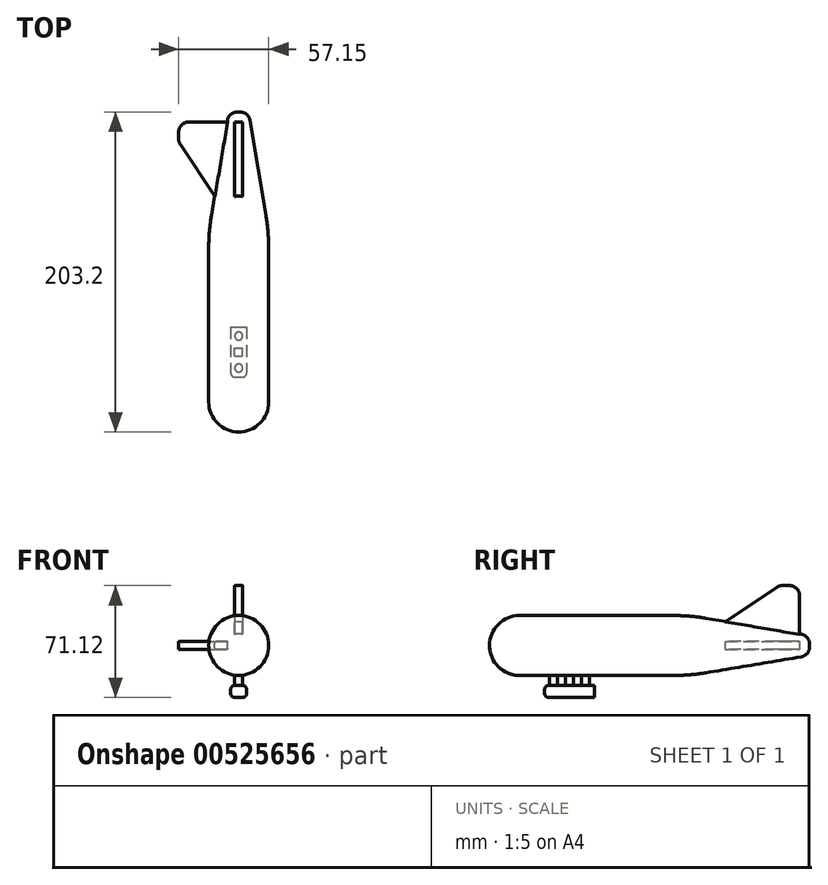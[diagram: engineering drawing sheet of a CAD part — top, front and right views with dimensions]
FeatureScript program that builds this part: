
annotation { "Feature Type Name" : "Feature", "Feature Type Description" : "" }
export const myFeature = defineFeature(function(context is Context, id is Id, definition is map)
    precondition{}
    {
        {
            var Q0;
            Q0=qCreatedBy(makeId("Front.planeOp"),FACE);
            var sketch = newSketch(context, id + "F0", { "sketchPlane" : qUnion([Q0])});
            skCircle(sketch, "E0", {"center": v(0, 0) * mm, "radius": 19.05 * mm});
            skSolve(sketch);
        }
        {
            var Q0;
            Q0=makeQuery(id+"F0.imprint","IMPRINT",FACE,{"disambiguationData":[TD([[makeQuery(id+"F0.imprint","IMPRINT",EDGE,{"derivedFrom":sQuery(id+"F0.wireOp",EDGE,"E0")}),1.0]])]});
            extrude(context, id + "F1", {"entities" : qUnion([Q0]), "endBound" : BoundingType.SYMMETRIC, "depth" : 203.2 * mm, "offsetDistance" : 25.4 * mm});
        }
        {
            var Q0;
            Q0=makeQuery(id+"F1.opExtrude","CAP_FACE",FACE,{"disambiguationData":[OSD([sQuery(id+"F0.wireOp",EDGE,"E0")])],"isStart":false});
            fillet(context, id + "F2", {"entities" : qUnion([Q0]), "radius" : 19.05 * mm, "tangentPropagation" : true, "allowEdgeOverflow" : false});
        }
        {
            var Q0;
            Q0=makeQuery(id+"F1.opExtrude","CAP_FACE",FACE,{"disambiguationData":[OSD([sQuery(id+"F0.wireOp",EDGE,"E0")])],"isStart":true});
            chamfer(context, id + "F3", {"entities" : qUnion([Q0]), "chamferType" : ChamferType.TWO_OFFSETS, "width1" : 76.2 * mm, "oppositeDirection" : false, "width2" : 12.7 * mm, "tangentPropagation" : true});
        }
        {
            var Q0;
            Q0=makeQuery(id+"F1.opExtrude","CAP_FACE",FACE,{"disambiguationData":[OSD([sQuery(id+"F0.wireOp",EDGE,"E0")])],"isStart":true});
            fillet(context, id + "F4", {"entities" : qUnion([Q0]), "radius" : 6.35 * mm, "tangentPropagation" : true, "allowEdgeOverflow" : false});
        }
        {
            var Q0;
            {var subQ0=sQuery(id+"F0.wireOp",EDGE,"E0");Q0=makeQuery(id+"F3.opChamfer","BLEND_EDGE",EDGE,{"blendedFrom":[makeQuery(id+"F1.opExtrude","CAP_EDGE",EDGE,{"disambiguationData":[OSD([subQ0])],"isStart":true}),makeQuery(id+"F1.opExtrude","SWEPT_FACE",FACE,{"disambiguationData":[OSD([subQ0])]})],"blendedInto":[makeQuery(id+"F1.opExtrude","SWEPT_FACE",FACE,{"disambiguationData":[OSD([subQ0])]})]});}
            fillet(context, id + "F5", {"entities" : qUnion([Q0]), "radius" : 127 * mm, "tangentPropagation" : true, "allowEdgeOverflow" : false});
        }
        {
            var Q0;
            Q0=qCreatedBy(makeId("Top.planeOp"),FACE);
            var sketch = newSketch(context, id + "F6", { "sketchPlane" : qUnion([Q0])});
            skLineSegment(sketch, "E1.bottom", {"start": v(-2.54, -48.26) * mm, "end": v(2.54, -48.26) * mm});
            skLineSegment(sketch, "E1.top", {"start": v(-2.54, -53.34) * mm, "end": v(2.54, -53.34) * mm});
            skLineSegment(sketch, "E1.left", {"start": v(-2.54, -48.26) * mm, "end": v(-2.54, -53.34) * mm});
            skLineSegment(sketch, "E1.right", {"start": v(2.54, -48.26) * mm, "end": v(2.54, -53.34) * mm});
            skPoint(sketch, "E1.middle", {"position": v(0, -50.8) * mm});
            skCircle(sketch, "E2", {"center": v(0, -60.96) * mm, "radius": 2.54 * mm});
            skCircle(sketch, "E3", {"center": v(0, -40.64) * mm, "radius": 2.54 * mm});
            skSolve(sketch);
        }
        {
            var Q0;
            Q0 = qSketchRegion(id + "F6", true);
            extrude(context, id + "F7", {"entities" : qUnion([Q0]), "operationType" : NewBodyOperationType.ADD, "oppositeDirection" : true, "depth" : 25.4 * mm, "offsetDistance" : 25.4 * mm});
        }
        {
            var Q0;
            Q0=makeQuery(id+"F7.opExtrude","CAP_FACE",FACE,{"disambiguationData":[OSD([sQuery(id+"F6.wireOp",EDGE,"E1.bottom"),sQuery(id+"F6.wireOp",EDGE,"E1.top"),sQuery(id+"F6.wireOp",EDGE,"E1.left"),sQuery(id+"F6.wireOp",EDGE,"E1.right")])],"isStart":false});
            var sketch = newSketch(context, id + "F8", { "sketchPlane" : qUnion([Q0])});
            skLineSegment(sketch, "E4.bottom", {"start": v(-5.08, 34.92) * mm, "end": v(5.08, 34.92) * mm});
            skLineSegment(sketch, "E4.top", {"start": v(-5.08, 66.67) * mm, "end": v(5.08, 66.67) * mm});
            skLineSegment(sketch, "E4.left", {"start": v(-5.08, 34.92) * mm, "end": v(-5.08, 66.67) * mm});
            skLineSegment(sketch, "E4.right", {"start": v(5.08, 34.92) * mm, "end": v(5.08, 66.67) * mm});
            skPoint(sketch, "E4.middle", {"position": v(0, 50.8) * mm});
            skPoint(sketch, "E4.middle.positionSnap0", {"position": v(2.54, 50.8) * mm});
            skPoint(sketch, "E4.middle.positionSnap1", {"position": v(0, 48.26) * mm});
            skPoint(sketch, "E4.centerSnap0", {"position": v(2.54, 50.8) * mm});
            skPoint(sketch, "E4.centerSnap1", {"position": v(0, 48.26) * mm});
            skSolve(sketch);
        }
        {
            var Q0;
            Q0 = qSketchRegion(id + "F8", true);
            extrude(context, id + "F9", {"entities" : qUnion([Q0]), "operationType" : NewBodyOperationType.ADD, "depth" : 7.62 * mm, "offsetDistance" : 25.4 * mm});
        }
        {
            var Q0;
            Q0=makeQuery(id+"F9.opExtrude","CAP_EDGE",EDGE,{"disambiguationData":[OSD([sQuery(id+"F8.wireOp",EDGE,"E4.left")])],"isStart":false});
            var Q1;
            Q1=makeQuery(id+"F9.opExtrude","CAP_EDGE",EDGE,{"disambiguationData":[OSD([sQuery(id+"F8.wireOp",EDGE,"E4.left")])],"isStart":true});
            var Q2;
            Q2=makeQuery(id+"F9.opExtrude","CAP_EDGE",EDGE,{"disambiguationData":[OSD([sQuery(id+"F8.wireOp",EDGE,"E4.right")])],"isStart":true});
            var Q3;
            Q3=makeQuery(id+"F9.opExtrude","CAP_EDGE",EDGE,{"disambiguationData":[OSD([sQuery(id+"F8.wireOp",EDGE,"E4.right")])],"isStart":false});
            fillet(context, id + "F10", {"entities" : qUnion([Q0, Q1, Q2, Q3]), "radius" : 2.54 * mm, "tangentPropagation" : true, "allowEdgeOverflow" : false});
        }
        {
            var Q0;
            Q0=makeQuery(id+"F9.opExtrude","SWEPT_FACE",FACE,{"disambiguationData":[OSD([sQuery(id+"F8.wireOp",EDGE,"E4.top")])]});
            fillet(context, id + "F11", {"entities" : qUnion([Q0]), "radius" : 2.54 * mm, "tangentPropagation" : true, "allowEdgeOverflow" : false});
        }
        {
            var Q0;
            Q0=qCreatedBy(makeId("Right.planeOp"),FACE);
            var sketch = newSketch(context, id + "F12", { "sketchPlane" : qUnion([Q0])});
            skLineSegment(sketch, "E5", {"start": v(25.4, 0) * mm, "end": v(95.25, 0) * mm});
            skLineSegment(sketch, "E6", {"start": v(95.25, 0) * mm, "end": v(95.25, 31.75) * mm});
            skLineSegment(sketch, "E7", {"start": v(88.9, 38.1) * mm, "end": v(84.47, 38.1) * mm});
            skLineSegment(sketch, "E8", {"start": v(80.95, 37.03) * mm, "end": v(25.4, 0) * mm});
            skPoint(sketch, "E9.visualSharp", {"position": v(95.25, 38.1) * mm});
            skArc(sketch, "E9.filletArc", {"start": v(95.25, 31.75) * mm, "mid": v(93.4, 36.24) * mm, "end": v(88.9, 38.1) * mm});
            skPoint(sketch, "E10.visualSharp", {"position": v(82.55, 38.1) * mm});
            skArc(sketch, "E10.filletArc", {"start": v(84.47, 38.1) * mm, "mid": v(82.63, 37.83) * mm, "end": v(80.95, 37.03) * mm});
            skSolve(sketch);
        }
        {
            var Q0;
            Q0 = qSketchRegion(id + "F12", true);
            extrude(context, id + "F13", {"entities" : qUnion([Q0]), "operationType" : NewBodyOperationType.ADD, "endBound" : BoundingType.SYMMETRIC, "depth" : 5.08 * mm, "offsetDistance" : 25.4 * mm});
        }
        {
            var Q0;
            Q0=qCreatedBy(makeId("Top.planeOp"),FACE);
            var sketch = newSketch(context, id + "F14", { "sketchPlane" : qUnion([Q0])});
            skLineSegment(sketch, "E11", {"start": v(0, 25.4) * mm, "end": v(0, 95.25) * mm});
            skLineSegment(sketch, "E12", {"start": v(0, 95.25) * mm, "end": v(-31.75, 95.25) * mm});
            skLineSegment(sketch, "E13", {"start": v(-38.1, 88.9) * mm, "end": v(-38.1, 84.47) * mm});
            skLineSegment(sketch, "E14", {"start": v(-37.03, 80.95) * mm, "end": v(0, 25.4) * mm});
            skPoint(sketch, "E15.visualSharp", {"position": v(-38.1, 95.25) * mm});
            skArc(sketch, "E15.filletArc", {"start": v(-31.75, 95.25) * mm, "mid": v(-36.24, 93.4) * mm, "end": v(-38.1, 88.9) * mm});
            skPoint(sketch, "E16.visualSharp", {"position": v(-38.1, 82.55) * mm});
            skArc(sketch, "E16.filletArc", {"start": v(-38.1, 84.47) * mm, "mid": v(-37.83, 82.63) * mm, "end": v(-37.03, 80.95) * mm});
            skSolve(sketch);
        }
        {
            var Q0;
            Q0 = qSketchRegion(id + "F14", true);
            extrude(context, id + "F15", {"entities" : qUnion([Q0]), "operationType" : NewBodyOperationType.ADD, "endBound" : BoundingType.SYMMETRIC, "depth" : 5.08 * mm, "offsetDistance" : 25.4 * mm});
        }
    });
